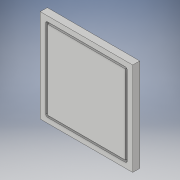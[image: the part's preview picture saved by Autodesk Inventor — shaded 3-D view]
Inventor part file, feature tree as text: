
AUTODESK INVENTOR PART (.ipt)
format: ipt  version: 2018 (Build 220112000, 112)  size: 109,568 bytes
history: native  units: in
note: dims shown in document units (in); Inventor stores cm internally (conversion verified against a paired STEP export)
features: extrude x1, sketch x1
ambient origin geometry x8: Origin, YZ Plane, XZ Plane, XY Plane, X Axis, Y Axis, Z Axis, Center Point
bodies: Solid1 (feature_tree)
feature tree (2):
  extrude  "Extrusion1"  Depth=5.14in
  sketch  "Sketch1"  dims[d0=5.06in d1=5.14in d2=6.02in d3=6.06in d4=0.125in d5=0.125in d6=0.459in d7=0.0in]
